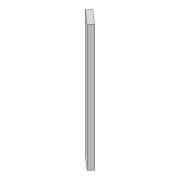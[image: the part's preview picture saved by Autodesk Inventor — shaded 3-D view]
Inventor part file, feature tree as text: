
AUTODESK INVENTOR PART (.ipt)
format: ipt  version: 2021 (Build 250183000, 183)  size: 106,496 bytes
history: native  units: in
note: dims shown in document units (in); Inventor stores cm internally (conversion verified against a paired STEP export)
features: extrude x1, sketch x1
ambient origin geometry x8: Origin, YZ Plane, XZ Plane, XY Plane, X Axis, Y Axis, Z Axis, Center Point
bodies: Body1 (feature_tree)
feature tree (2):
  extrude  "Extrusion2"  Depth=118.1102in TaperAngle=360.0deg
  sketch  "Sketch1"  dims[d0=118.1102in d1=6.2992in d3=360.0deg d7=1968.5039in d8=1.5748in d10=360.0deg d12=3.0in d14=5.0in d15=16.7359in d16=118.1102in d17=0.0in]
